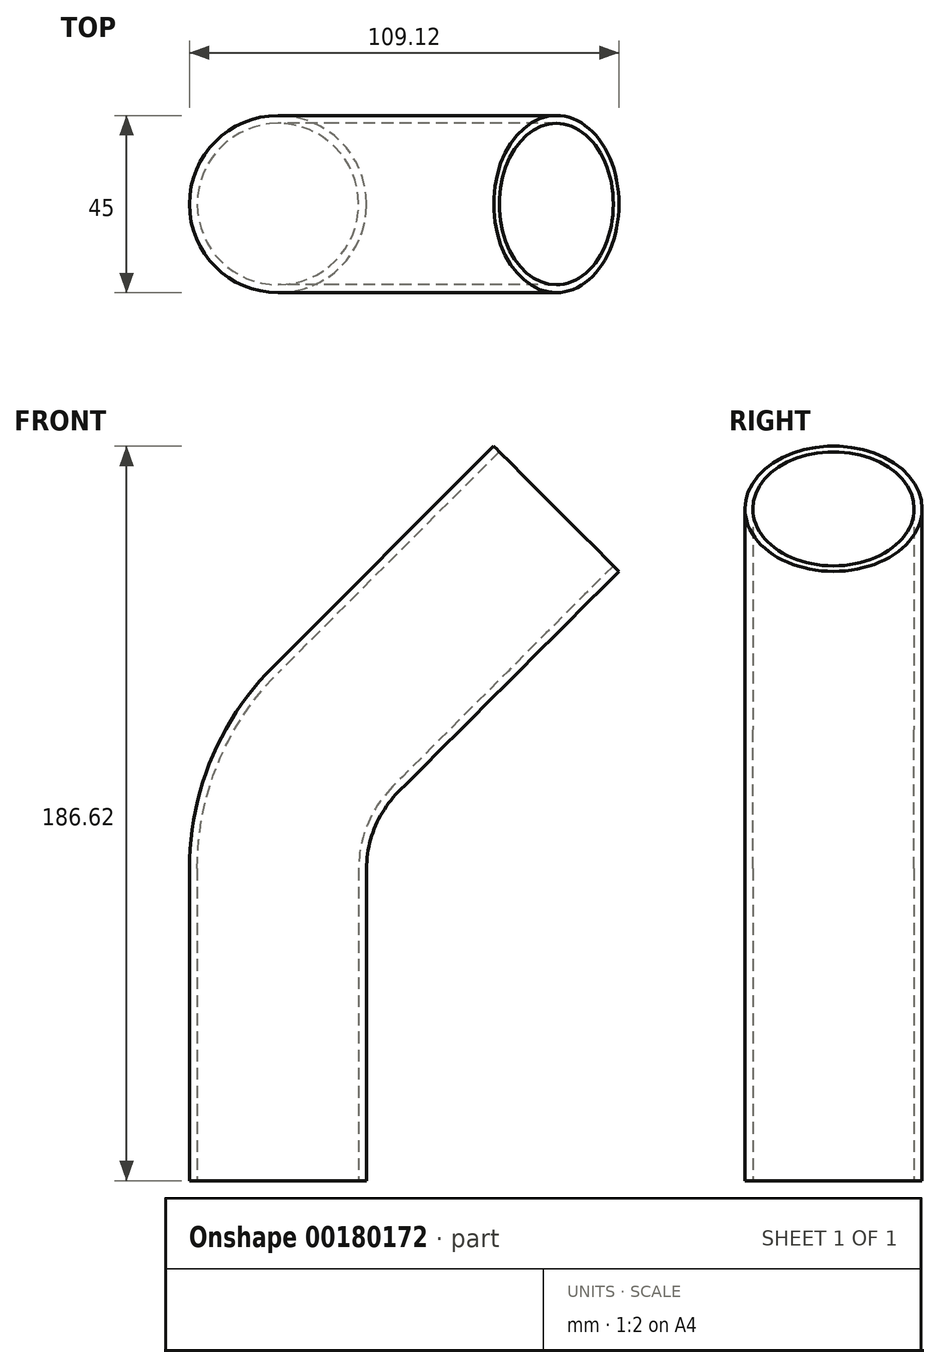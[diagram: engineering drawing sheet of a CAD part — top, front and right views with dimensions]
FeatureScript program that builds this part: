
annotation { "Feature Type Name" : "Feature", "Feature Type Description" : "" }
export const myFeature = defineFeature(function(context is Context, id is Id, definition is map)
    precondition{}
    {
        {
            var Q0;
            Q0=qCreatedBy(makeId("Front.planeOp"),FACE);
            var sketch = newSketch(context, id + "F0", { "sketchPlane" : qUnion([Q0])});
            skLineSegment(sketch, "E0", {"start": v(0, 0) * mm, "end": v(0, 79.29) * mm});
            skLineSegment(sketch, "E1", {"start": v(14.64, 114.64) * mm, "end": v(70.71, 170.71) * mm});
            skPoint(sketch, "E2.visualSharp", {"position": v(0, 100) * mm});
            skArc(sketch, "E2.filletArc", {"start": v(14.64, 114.64) * mm, "mid": v(3.8, 98.42) * mm, "end": v(0, 79.29) * mm});
            skSolve(sketch);
        }
        {
            var Q0;
            Q0=sQuery(id+"F0.wireOp",VERTEX,"E1.end");
            var Q1;
            Q1=qCreatedBy(makeId("Top.planeOp"),FACE);
            cPlane(context, id + "F1", {"entities" : qUnion([Q0, Q1]), "cplaneType" : CPlaneType.PLANE_POINT, "offset" : 25 * mm, "width" : 150 * mm, "height" : 150 * mm});
        }
        {
            var Q0;
            Q0=qCreatedBy(id+"F1.planeOp",FACE);
            var sketch = newSketch(context, id + "F2", { "sketchPlane" : qUnion([Q0])});
            skLineSegment(sketch, "E3", {"start": v(70.71, 46.02) * mm, "end": v(70.71, -46.02) * mm});
            skSolve(sketch);
        }
        {
            var Q0;
            Q0=sQuery(id+"F2.wireOp",EDGE,"E3");
            var Q1;
            Q1=qCreatedBy(makeId("Top.planeOp"),FACE);
            cPlane(context, id + "F3", {"entities" : qUnion([Q0, Q1]), "cplaneType" : CPlaneType.LINE_ANGLE, "offset" : 25 * mm, "angle" : 135 * degree, "width" : 150 * mm, "height" : 150 * mm});
        }
        {
            var Q0;
            Q0=qCreatedBy(id+"F3.planeOp",FACE);
            var sketch = newSketch(context, id + "F4", { "sketchPlane" : qUnion([Q0])});
            skPoint(sketch, "E4.0", {"position": v(0, 70.71) * mm});
            skCircle(sketch, "E5", {"center": v(0, 70.71) * mm, "radius": 22.5 * mm});
            skCircle(sketch, "E6.0", {"center": v(0, 70.71) * mm, "radius": 20.5 * mm});
            skSolve(sketch);
        }
        {
            var Q0;
            Q0=makeQuery(id+"F4.imprint","IMPRINT",FACE,{"disambiguationData":[TD([[makeQuery(id+"F4.imprint","IMPRINT",EDGE,{"derivedFrom":sQuery(id+"F4.wireOp",EDGE,"E5")}),1.0]])]});
            var Q1;
            Q1=sQuery(id+"F0.wireOp",EDGE,"E1");
            var Q2;
            Q2=sQuery(id+"F0.wireOp",EDGE,"E2.filletArc");
            var Q3;
            Q3=sQuery(id+"F0.wireOp",EDGE,"E0");
            sweep(context, id + "F5", {"profiles" : qUnion([Q0]), "path" : qUnion([Q1, Q2, Q3])});
        }
    });
